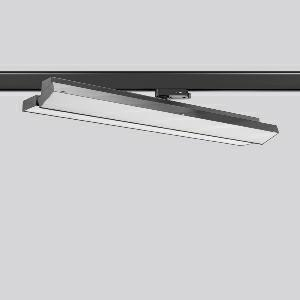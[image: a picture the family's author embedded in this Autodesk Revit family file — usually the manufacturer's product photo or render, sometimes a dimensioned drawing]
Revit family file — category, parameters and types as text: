
# Revit family: tx-move_742164_003_2_0653
name_source: partatom
category: Lighting Fixtures
units: mm (PartAtom-declared; Revit-internal decimal feet)

## family parameters
Cut with Voids When Loaded = No
Host = Face
Light Source = No
Part Type = Normal
Room Calculation Point = No
Round Connector Dimension = Use Diameter
Shared = No

## types (1)
- MultiLumen 1 (1 x LED Modul 927, 1800 lm, 2700)
    Apparent Load = 38 VA
    CIE Flux Codes = 47 79 96 100 100
    Color Rendering = 92
    Color Temperature = 2700
    Default Elevation = 1800 mm  [stored 5.90551 ft]
    Description = Series: TX-MOVE
Multifunctional surface-mounted spotlight for area lighting. Very flat design. Housing: sheet steel, powder-coated. Rotation range: 356°. Swivel range: 90°. Consistent alignment possible with visible tilt scale. High-efficiency LED units with flush-mounted opal diffuser made of non-yellowing PMMA. Symmetrical wide beam light distribution. Best colour rendering with CRI >90 for fresh products and coloured textiles. With multi adaptor for 3-circuit tracks 230 V. Suitable for Track on ceiling. MultiLumen: Luminous flux adjustable in 3 steps. Factory setting is the highest luminous flux. Environmentally friendly and resource-saving due to replaceable and recyclable components. 
Colour: deep black, matt (RAL 9005)
Length: 570 mm
Width: 119 mm
Height: 92 mm
Lamp: LED
Socket: without socket
Colour temperature: 2700K
Colour rendering index (CRI): 90
System power: 38 W
Rated luminous flux: 3600 lm
Luminous efficiency: 95 lm/W
System power 2: 51 W
Rated luminous flux 2: 4700 lm
Luminous efficiency 2: 92 lm/W
System power 3: 62 W
Rated luminous flux 3: 5550 lm
Luminous efficiency 3: 90 lm/W
Control gear: Regulated power supply
Protection class: I
Type of protection: IP 20
    Height = 75 mm
    Lamp = 1 x LED Modul 927
    Lamp Light Flux = 1800 lm
    Lamp count = 1
    Length = 569 mm
    Lifetime = 50000 h
    Luminous efficacy = 95 lm/W
    Manufacturer = RZB
    ModVariant = No
    Model = 742164.003.2
    Mounting Place = Ceiling
    Mounting Type = Surface mounted
    Number of Poles = 1
    OnlyDefault = Yes
    Power Factor = 1
    Product Name = TX-MOVE
    Product group = Track mounted projectors
    ProductGroupID = 301
    Protection Class = Protection class I
    Protection Degree = IP 20
    RLX_Detail_Level = 1
    RLX_Emergency_Light_Flux = 0 lm
    RLX_Emergency_Type = 0
    RLX_Emergency_Type_DB = No
    RlxData = <blob elided: 35805 chars, md5=0a9c8f3a>
    Socket = socket
    Standby Power = 0 W
    System Light Flux = 3600 lm
    System Power = 38 W
    Type Comments = MultiLumen 1
    Type Image = 742164.003.jpg
    URL = http://relux.com
    VarID = multilumen_1
    Voltage = 0 V
    Weight = 0.00 kg
    Width = 119 mm

note: [stored X ft] marks values corroborated as IEEE doubles in the binary element streams (Revit-internal decimal feet)

## geometry (parser evidence)
native form markers: Blend x4, Sweep x15
no freeform markers — native parametric forms only
